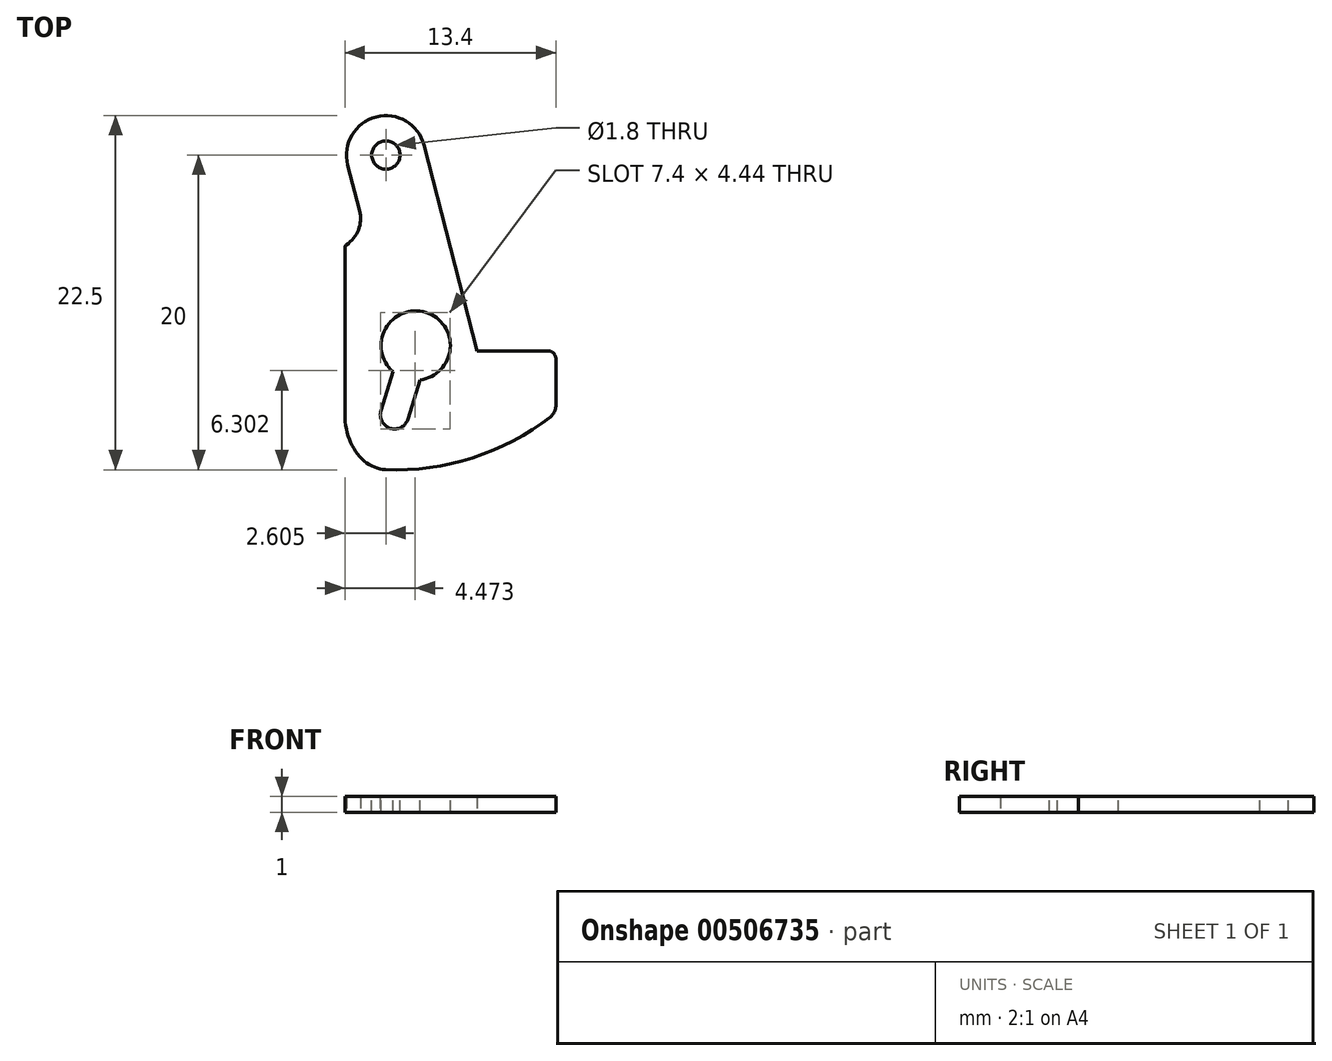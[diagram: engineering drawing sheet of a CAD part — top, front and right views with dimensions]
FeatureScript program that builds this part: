
annotation { "Feature Type Name" : "Feature", "Feature Type Description" : "" }
export const myFeature = defineFeature(function(context is Context, id is Id, definition is map)
    precondition{}
    {
        {
            var Q0;
            Q0=qCreatedBy(makeId("Top.planeOp"),FACE);
            var sketch = newSketch(context, id + "F0", { "sketchPlane" : qUnion([Q0])});
            skLineSegment(sketch, "E0.bottom", {"start": v(0, 0) * mm, "end": v(13.4, 0) * mm, "construction": true});
            skLineSegment(sketch, "E0.top", {"start": v(0, 22.5) * mm, "end": v(13.4, 22.5) * mm, "construction": true});
            skLineSegment(sketch, "E0.left", {"start": v(0, 0) * mm, "end": v(0, 22.5) * mm, "construction": true});
            skLineSegment(sketch, "E0.right", {"start": v(13.4, 0) * mm, "end": v(13.4, 22.5) * mm, "construction": true});
            skCircle(sketch, "E1", {"center": v(2.6, 20) * mm, "radius": 0.75 * mm});
            skArc(sketch, "E2", {"start": v(5.03, 20.63) * mm, "mid": v(1.98, 22.42) * mm, "end": v(0.18, 19.37) * mm});
            skLineSegment(sketch, "E3", {"start": v(5.03, 20.63) * mm, "end": v(8.4, 7.56) * mm});
            skLineSegment(sketch, "E4", {"start": v(8.4, 7.56) * mm, "end": v(12.9, 7.56) * mm});
            skLineSegment(sketch, "E5", {"start": v(0.18, 19.37) * mm, "end": v(0.94, 16.47) * mm});
            skArc(sketch, "E6", {"start": v(0.94, 16.47) * mm, "mid": v(0.87, 15.24) * mm, "end": v(0.1, 14.3) * mm});
            skArc(sketch, "E7", {"start": v(4.84, 5.93) * mm, "mid": v(5.09, 9.8) * mm, "end": v(3.12, 6.45) * mm});
            skArc(sketch, "E8", {"start": v(2.29, 3.76) * mm, "mid": v(2.89, 2.64) * mm, "end": v(4.01, 3.24) * mm});
            skCircle(sketch, "E9", {"center": v(4.5, 7.9) * mm, "radius": 0.9 * mm, "construction": true});
            skLineSegment(sketch, "E10", {"start": v(2.29, 3.76) * mm, "end": v(3.12, 6.45) * mm});
            skLineSegment(sketch, "E11", {"start": v(5.36, 7.63) * mm, "end": v(4.84, 5.93) * mm, "construction": true});
            skLineSegment(sketch, "E12", {"start": v(4.84, 5.93) * mm, "end": v(4.01, 3.24) * mm});
            skLineSegment(sketch, "E13", {"start": v(3.12, 6.45) * mm, "end": v(3.64, 8.16) * mm, "construction": true});
            skLineSegment(sketch, "E14", {"start": v(4.5, 7.9) * mm, "end": v(5.09, 9.8) * mm, "construction": true});
            skLineSegment(sketch, "E15", {"start": v(3.15, 3.5) * mm, "end": v(2.89, 2.64) * mm, "construction": true});
            skLineSegment(sketch, "E16", {"start": v(2.25, 3.5) * mm, "end": v(0, 3.5) * mm, "construction": true});
            skLineSegment(sketch, "E17", {"start": v(2.5, 7.9) * mm, "end": v(0, 7.9) * mm, "construction": true});
            skLineSegment(sketch, "E18", {"start": v(8.08, 8.83) * mm, "end": v(6.44, 8.4) * mm, "construction": true});
            skLineSegment(sketch, "E19", {"start": v(4.2, 9.87) * mm, "end": v(2.72, 19.26) * mm, "construction": true});
            skLineSegment(sketch, "E20", {"start": v(13.4, 7.06) * mm, "end": v(13.4, 4.06) * mm});
            skArc(sketch, "E21", {"start": v(13.06, 3.37) * mm, "mid": v(13.31, 3.67) * mm, "end": v(13.4, 4.06) * mm});
            skArc(sketch, "E22", {"start": v(2.58, 0.01) * mm, "mid": v(8.12, 0.76) * mm, "end": v(13.06, 3.37) * mm});
            skLineSegment(sketch, "E23", {"start": v(12.53, 4.06) * mm, "end": v(13.4, 4.06) * mm, "construction": true});
            skEllipticalArc(sketch, "E24", {});
            skLineSegment(sketch, "E25", {"start": v(0, 14.12) * mm, "end": v(0, 3.53) * mm});
            skLineSegment(sketch, "E26", {"start": v(2.58, 0.01) * mm, "end": v(13.06, 3.37) * mm, "construction": true});
            skLineSegment(sketch, "E27", {"start": v(3.15, 3.5) * mm, "end": v(3.15, 0) * mm, "construction": true});
            skPoint(sketch, "E28.visualSharp", {"position": v(13.4, 7.56) * mm});
            skArc(sketch, "E28.filletArc", {"start": v(13.4, 7.06) * mm, "mid": v(13.25, 7.41) * mm, "end": v(12.9, 7.56) * mm});
            skPoint(sketch, "E29.visualSharp", {"position": v(0, 14.23) * mm});
            skArc(sketch, "E29.filletArc", {"start": v(0.1, 14.3) * mm, "mid": v(0.02, 14.22) * mm, "end": v(0, 14.12) * mm});
            const initialGuessF0  = {"E24": [0.002664624674916654, 0.0035349456811931633, 0, -1, 0.003523901289118902, 0.0026646246749166516, 4.71238898038469, 6.253191349905612]};
            skSetInitialGuess(sketch, initialGuessF0);
            skSolve(sketch);
        }
        {
            var Q0;
            Q0 = qSketchRegion(id + "F0", true);
            extrude(context, id + "F1", {"entities" : qUnion([Q0]), "depth" : 1 * mm});
        }
        {
            var Q0;
            Q0=makeQuery(id+"F1.opExtrude","CAP_FACE",FACE,{"disambiguationData":[OSD([sQuery(id+"F0.wireOp",EDGE,"E1"),sQuery(id+"F0.wireOp",EDGE,"E2"),sQuery(id+"F0.wireOp",EDGE,"E3"),sQuery(id+"F0.wireOp",EDGE,"E4"),sQuery(id+"F0.wireOp",EDGE,"E5"),sQuery(id+"F0.wireOp",EDGE,"E6"),sQuery(id+"F0.wireOp",EDGE,"E7"),sQuery(id+"F0.wireOp",EDGE,"E8"),sQuery(id+"F0.wireOp",EDGE,"E10"),sQuery(id+"F0.wireOp",EDGE,"E12"),sQuery(id+"F0.wireOp",EDGE,"E20"),sQuery(id+"F0.wireOp",EDGE,"E21"),sQuery(id+"F0.wireOp",EDGE,"E22"),sQuery(id+"F0.wireOp",EDGE,"E24"),sQuery(id+"F0.wireOp",EDGE,"E25"),sQuery(id+"F0.wireOp",EDGE,"E28.filletArc"),sQuery(id+"F0.wireOp",EDGE,"E29.filletArc")])],"isStart":false});
            var sketch = newSketch(context, id + "F2", { "sketchPlane" : qUnion([Q0])});
            skCircle(sketch, "E30", {"center": v(4.5, 7.9) * mm, "radius": 2.2 * mm});
            skCircle(sketch, "E31", {"center": v(3.15, 3.5) * mm, "radius": 1 * mm});
            skCircle(sketch, "E32", {"center": v(4.5, 7.9) * mm, "radius": 1 * mm});
            skLineSegment(sketch, "E33", {"start": v(3.54, 8.2) * mm, "end": v(2.2, 3.8) * mm});
            skLineSegment(sketch, "E34", {"start": v(5.46, 7.6) * mm, "end": v(4.1, 3.2) * mm});
            skCircle(sketch, "E35", {"center": v(2.6, 20) * mm, "radius": 0.9 * mm});
            skSolve(sketch);
        }
        {
            var Q0;
            {var subQ5=makeQuery(id+"F1.opExtrude","CAP_EDGE",EDGE,{"disambiguationData":[OSD([sQuery(id+"F0.wireOp",EDGE,"E10")])],"isStart":false});var subQ10=sQuery(id+"F2.wireOp",EDGE,"E30");var subQ11=makeQuery(id+"F2.imprint","INTERSECT",VERTEX,{"derivedFrom":[subQ5,subQ10]});Q0=makeQuery(id+"F2.imprint","IMPRINT",FACE,{"disambiguationData":[TD([[makeQuery(id+"F2.imprint","IMPRINT",EDGE,{"disambiguationData":[TD([[subQ11,-1.0]])],"derivedFrom":subQ10}),1.0]])]});}
            var Q1;
            {var subQ0=sQuery(id+"F2.wireOp",EDGE,"E33");var subQ1=sQuery(id+"F2.wireOp",EDGE,"E30");var subQ2=makeQuery(id+"F2.imprint","INTERSECT",VERTEX,{"derivedFrom":[subQ1,subQ0]});Q1=makeQuery(id+"F2.imprint","IMPRINT",FACE,{"disambiguationData":[TD([[makeQuery(id+"F2.imprint","IMPRINT",EDGE,{"disambiguationData":[TD([[subQ2,1.0]])],"derivedFrom":subQ1}),1.0]])]});}
            var Q2;
            {var subQ0=sQuery(id+"F2.wireOp",EDGE,"E34");var subQ1=sQuery(id+"F2.wireOp",EDGE,"E30");var subQ2=makeQuery(id+"F2.imprint","INTERSECT",VERTEX,{"derivedFrom":[subQ1,subQ0]});Q2=makeQuery(id+"F2.imprint","IMPRINT",FACE,{"disambiguationData":[TD([[makeQuery(id+"F2.imprint","IMPRINT",EDGE,{"disambiguationData":[TD([[subQ2,1.0]])],"derivedFrom":subQ1}),1.0]])]});}
            var Q3;
            {var subQ0=sQuery(id+"F2.wireOp",EDGE,"E33");var subQ1=sQuery(id+"F2.wireOp",EDGE,"E30");var subQ2=makeQuery(id+"F2.imprint","INTERSECT",VERTEX,{"derivedFrom":[subQ1,subQ0]});Q3=makeQuery(id+"F2.imprint","IMPRINT",FACE,{"disambiguationData":[TD([[makeQuery(id+"F2.imprint","IMPRINT",EDGE,{"disambiguationData":[TD([[subQ2,-1.0]])],"derivedFrom":subQ1}),1.0]])]});}
            var Q4;
            {var subQ0=sQuery(id+"F2.wireOp",EDGE,"E33");var subQ1=sQuery(id+"F2.wireOp",EDGE,"E32");var subQ2=makeQuery(id+"F2.imprint","INTERSECT",VERTEX,{"derivedFrom":[subQ1,subQ0]});Q4=makeQuery(id+"F2.imprint","IMPRINT",FACE,{"disambiguationData":[TD([[makeQuery(id+"F2.imprint","IMPRINT",EDGE,{"disambiguationData":[TD([[subQ2,1.0]])],"derivedFrom":subQ1}),-1.0]])]});}
            extrude(context, id + "F3", {"entities" : qUnion([Q0, Q1, Q2, Q3, Q4]), "operationType" : NewBodyOperationType.REMOVE, "endBound" : BoundingType.THROUGH_ALL, "oppositeDirection" : true, "depth" : 25 * mm});
        }
        {
            var Q0;
            Q0=makeQuery(id+"F2.imprint","IMPRINT",FACE,{"disambiguationData":[TD([[makeQuery(id+"F2.imprint","IMPRINT",EDGE,{"derivedFrom":sQuery(id+"F2.wireOp",EDGE,"E35")}),1.0]])]});
            extrude(context, id + "F4", {"entities" : qUnion([Q0]), "operationType" : NewBodyOperationType.REMOVE, "endBound" : BoundingType.THROUGH_ALL, "oppositeDirection" : true, "depth" : 25 * mm});
        }
    });
